# Revit family: Civil_Drainage_ACO_StormBrixx_Additional_Inspection_Point wm
name_source: partatom
category: Generic Models
revit_build: Autodesk Revit 2013 (Build: 20120221_2030(x64)
units: mm (PartAtom-declared; Revit-internal decimal feet)

## types (1)
- Civil_Drainage_ACO_StormBrixx_Additional_Inspection_Point wm
    Assembly Code = D2090300
    Cost = 0 $
    Current Revision = 1
    Depth = 180 mm
    Description = Inspection Point Module
    Distributed by = www.aco.co.uk
    Fax = +44 (0)1462 815895
    Inspection Connector Colour = Black
    Inspection Connector Dimensions = 600mm x 600mm x 200mm (L x W x H)
    Inspection Connector Material = Polypropylene
    Inspection Connector Product Code = 27018
    Inspection Connector Recyclable = Fully Recyclable
    Inspection Connector Recycled Material Content = 0%
    Inspection Connector Weight (kg) = 2.5
    Inspection Cover Colour = Black
    Inspection Cover Dimensions = 410mm x 410mm x 180mm (L x W x H)
    Inspection Cover Material = Ductile Iron
    Inspection Cover Product Code = 314045
    Inspection Cover Recyclable = Fully Recyclable
    Inspection Cover Recycled Material Content = Between 40% - 90%
    Inspection Cover Weight (kg) = 52
    Installation Guidelines = http://www.aco.co.uk
    Keynote = R17:315
    Length = 600 mm
    Maintenance Guidelines = http://www.aco.co.uk
    Manufacturer = ACO Technologies plc
    Model = Inspection Point Module
    Product Range = ACO StormBrixx
    Product Type = Stormwater attenuation & infiltration
    Product Website = www.stormbrixx.co.uk
    Telephone = +44 (0)1462 816666
    Type Comments = Inspection Point Module
    URL = www.aco.co.uk
    piping = ACO_Plastic_Black

## geometry (parser evidence)
native form markers: Blend x4, Sweep x3
no freeform markers — native parametric forms only
